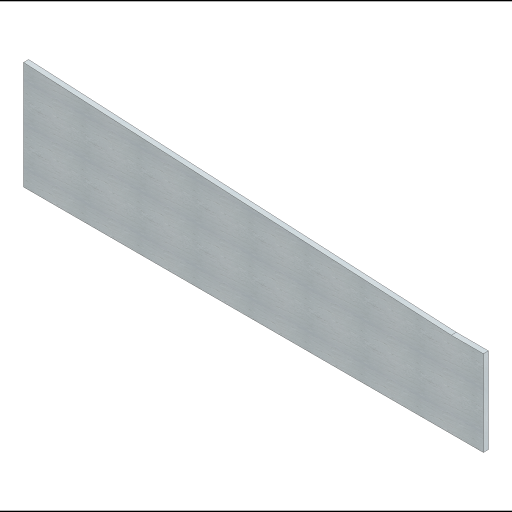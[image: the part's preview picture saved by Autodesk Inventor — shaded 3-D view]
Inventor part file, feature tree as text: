
AUTODESK INVENTOR PART (.ipt)
format: ipt  version: 2023 (Build 270158000, 158)  size: 251,392 bytes
history: native  units: in
note: dims shown in document units (in); Inventor stores cm internally (conversion verified against a paired STEP export)
features: extrude x1, sketch x1
ambient origin geometry x8: Origin, YZ Plane, XZ Plane, XY Plane, X Axis, Y Axis, Z Axis, Center Point
bodies: Solid1 (feature_tree)
feature tree (2):
  extrude  "Extrusion1"  Depth=3.0in
  sketch  "Sketch1"  dims[d0=8.0in d1=3.0in d2=0.0206in d3=40.0in d4=0.47in d5=0.0in]
